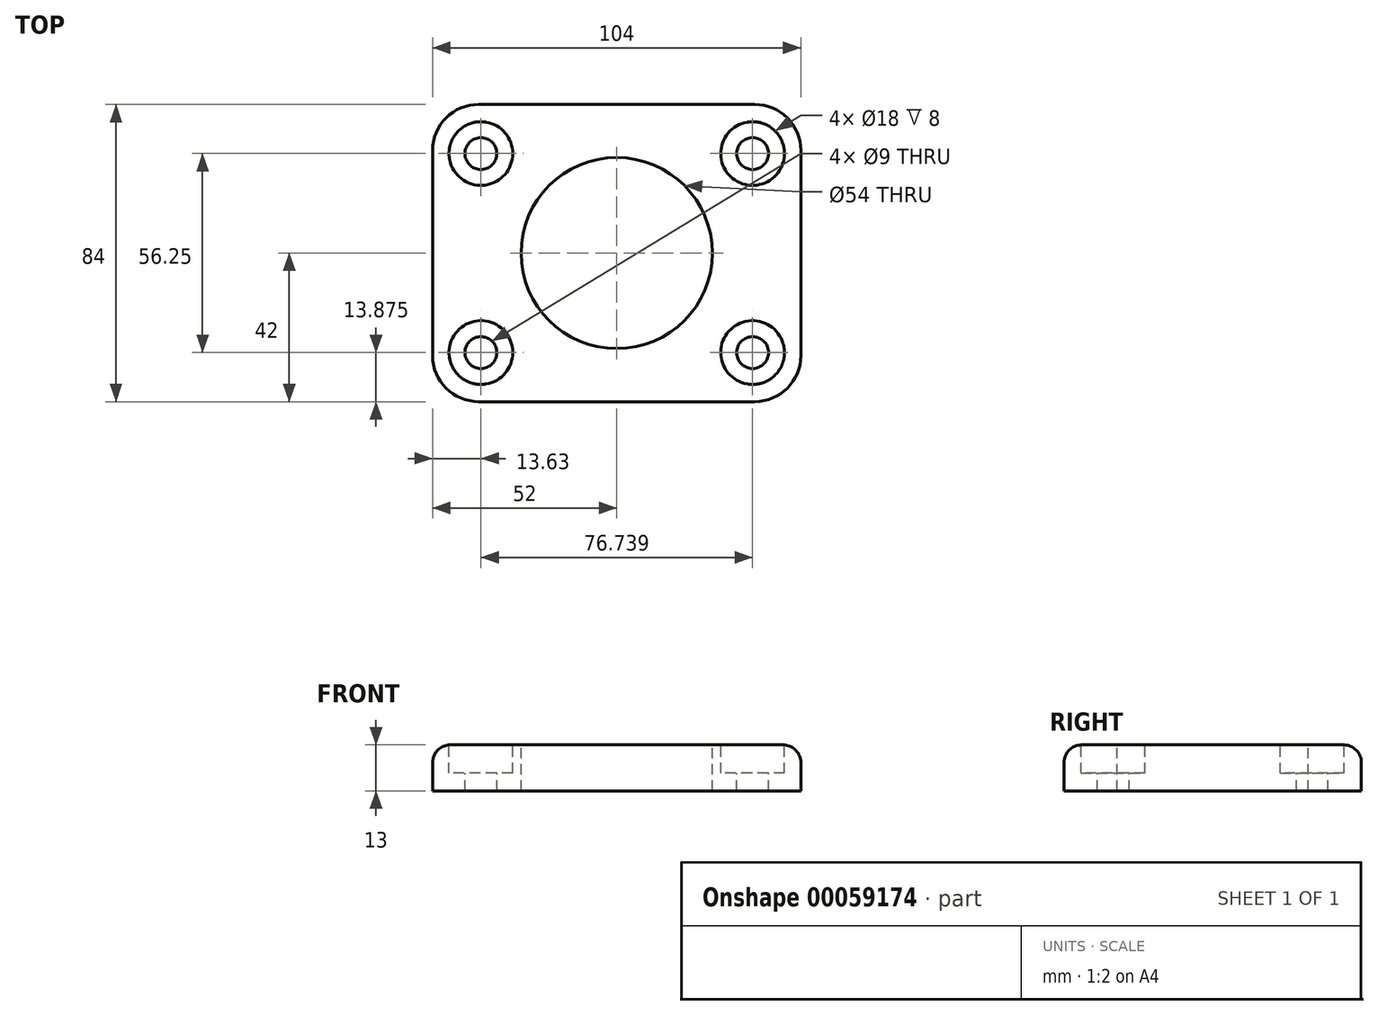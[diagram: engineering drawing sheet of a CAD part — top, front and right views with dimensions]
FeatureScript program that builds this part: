
annotation { "Feature Type Name" : "Feature", "Feature Type Description" : "" }
export const myFeature = defineFeature(function(context is Context, id is Id, definition is map)
    precondition{}
    {
        {
            var Q0;
            Q0=qCreatedBy(makeId("Top.planeOp"),FACE);
            var sketch = newSketch(context, id + "F0", { "sketchPlane" : qUnion([Q0])});
            skLineSegment(sketch, "E0.rect.bottom", {"start": v(52, 42) * mm, "end": v(-52, 42) * mm});
            skLineSegment(sketch, "E0.rect.top", {"start": v(52, -42) * mm, "end": v(-52, -42) * mm});
            skLineSegment(sketch, "E0.rect.left", {"start": v(52, 42) * mm, "end": v(52, -42) * mm});
            skLineSegment(sketch, "E0.rect.right", {"start": v(-52, 42) * mm, "end": v(-52, -42) * mm});
            skPoint(sketch, "E0.rect.middle", {"position": v(0, 0) * mm});
            skPoint(sketch, "E1", {"position": v(32, 27) * mm});
            skSolve(sketch);
        }
        {
            var Q0;
            Q0=makeQuery(id+"F0.imprint","IMPRINT",FACE,{"disambiguationData":[TD([[makeQuery(id+"F0.imprint","IMPRINT",EDGE,{"derivedFrom":sQuery(id+"F0.wireOp",EDGE,"E0.rect.bottom")}),1.0]])]});
            extrude(context, id + "F1", {"entities" : qUnion([Q0]), "oppositeDirection" : true, "depth" : 13 * mm});
        }
        {
            var Q0;
            Q0=makeQuery(id+"F1.opExtrude","CAP_FACE",FACE,{"disambiguationData":[OSD([sQuery(id+"F0.wireOp",EDGE,"E0.rect.bottom"),sQuery(id+"F0.wireOp",EDGE,"E0.rect.top"),sQuery(id+"F0.wireOp",EDGE,"E0.rect.left"),sQuery(id+"F0.wireOp",EDGE,"E0.rect.right")])],"isStart":true});
            var sketch = newSketch(context, id + "F2", { "sketchPlane" : qUnion([Q0])});
            skLineSegment(sketch, "E2", {"start": v(35.49, 25) * mm, "end": v(41.25, 31.25) * mm});
            skArc(sketch, "E3.0.startCap", {"start": v(38.8, 21.95) * mm, "mid": v(32.44, 21.7) * mm, "end": v(32.18, 28.05) * mm});
            skArc(sketch, "E3.0.endCap", {"start": v(37.94, 34.3) * mm, "mid": v(44.3, 34.56) * mm, "end": v(44.56, 28.2) * mm});
            skLineSegment(sketch, "E3.0.left", {"start": v(32.18, 28.05) * mm, "end": v(37.94, 34.3) * mm});
            skLineSegment(sketch, "E3.0.right", {"start": v(38.8, 21.95) * mm, "end": v(44.56, 28.2) * mm});
            skArc(sketch, "E4.MirrorCS", {"start": v(38.8, -21.95) * mm, "mid": v(32.44, -21.7) * mm, "end": v(32.18, -28.05) * mm});
            skLineSegment(sketch, "E5.MirrorCS", {"start": v(35.49, -25) * mm, "end": v(41.25, -31.25) * mm});
            skLineSegment(sketch, "E6.MirrorCS", {"start": v(32.18, -28.05) * mm, "end": v(37.94, -34.3) * mm});
            skLineSegment(sketch, "E7.MirrorCS", {"start": v(38.8, -21.95) * mm, "end": v(44.56, -28.2) * mm});
            skArc(sketch, "E8.MirrorCS", {"start": v(37.94, -34.3) * mm, "mid": v(44.3, -34.56) * mm, "end": v(44.56, -28.2) * mm});
            skLineSegment(sketch, "E9.MirrorCS", {"start": v(-38.8, -21.95) * mm, "end": v(-44.56, -28.2) * mm});
            skArc(sketch, "E10.MirrorCS", {"start": v(-37.94, -34.3) * mm, "mid": v(-44.3, -34.56) * mm, "end": v(-44.56, -28.2) * mm});
            skLineSegment(sketch, "E11.MirrorCS", {"start": v(-32.18, -28.05) * mm, "end": v(-37.94, -34.3) * mm});
            skArc(sketch, "E12.MirrorCS", {"start": v(-37.94, 34.3) * mm, "mid": v(-44.3, 34.56) * mm, "end": v(-44.56, 28.2) * mm});
            skLineSegment(sketch, "E13.MirrorCS", {"start": v(-35.49, -25) * mm, "end": v(-41.25, -31.25) * mm});
            skLineSegment(sketch, "E14.MirrorCS", {"start": v(-35.49, 25) * mm, "end": v(-41.25, 31.25) * mm});
            skArc(sketch, "E15.MirrorCS", {"start": v(-38.8, 21.95) * mm, "mid": v(-32.44, 21.7) * mm, "end": v(-32.18, 28.05) * mm});
            skArc(sketch, "E16.MirrorCS", {"start": v(-38.8, -21.95) * mm, "mid": v(-32.44, -21.7) * mm, "end": v(-32.18, -28.05) * mm});
            skLineSegment(sketch, "E17.MirrorCS", {"start": v(-38.8, 21.95) * mm, "end": v(-44.56, 28.2) * mm});
            skLineSegment(sketch, "E18.MirrorCS", {"start": v(-32.18, 28.05) * mm, "end": v(-37.94, 34.3) * mm});
            skSolve(sketch);
        }
        {
            var Q0;
            Q0=qCreatedBy(makeId("Top.planeOp"),FACE);
            var sketch = newSketch(context, id + "F3", { "sketchPlane" : qUnion([Q0])});
            skCircle(sketch, "E19", {"center": v(38.37, 28.13) * mm, "radius": 9 * mm});
            skCircle(sketch, "E20", {"center": v(38.37, -28.13) * mm, "radius": 9 * mm});
            skCircle(sketch, "E21", {"center": v(-38.37, 28.13) * mm, "radius": 9 * mm});
            skCircle(sketch, "E22", {"center": v(-38.37, -28.13) * mm, "radius": 9 * mm});
            skSolve(sketch);
        }
        {
            var Q0;
            Q0 = qSketchRegion(id + "F3", true);
            extrude(context, id + "F4", {"entities" : qUnion([Q0]), "operationType" : NewBodyOperationType.REMOVE, "oppositeDirection" : true, "depth" : 8 * mm});
        }
        {
            var Q0;
            Q0=makeQuery(id+"F4.boolean.opBoolean","COPY",FACE,{"derivedFrom":makeQuery(id+"F4.opExtrude","CAP_FACE",FACE,{"disambiguationData":[OSD([sQuery(id+"F3.wireOp",EDGE,"E19")])],"isStart":false})});
            var sketch = newSketch(context, id + "F5", { "sketchPlane" : qUnion([Q0])});
            skCircle(sketch, "E23", {"center": v(38.37, 28.13) * mm, "radius": 4.5 * mm});
            skCircle(sketch, "E24", {"center": v(38.37, -28.13) * mm, "radius": 4.5 * mm});
            skCircle(sketch, "E25", {"center": v(-38.37, 28.13) * mm, "radius": 4.5 * mm});
            skCircle(sketch, "E26", {"center": v(-38.37, -28.13) * mm, "radius": 4.5 * mm});
            skSolve(sketch);
        }
        {
            var Q0;
            Q0 = qSketchRegion(id + "F5", true);
            extrude(context, id + "F6", {"entities" : qUnion([Q0]), "operationType" : NewBodyOperationType.REMOVE, "oppositeDirection" : true, "depth" : 25 * mm});
        }
        {
            var Q0;
            Q0=qCreatedBy(makeId("Top.planeOp"),FACE);
            var sketch = newSketch(context, id + "F7", { "sketchPlane" : qUnion([Q0])});
            skCircle(sketch, "E27", {"center": v(0, 0) * mm, "radius": 27 * mm});
            skSolve(sketch);
        }
        {
            var Q0;
            Q0 = qSketchRegion(id + "F7", true);
            extrude(context, id + "F8", {"entities" : qUnion([Q0]), "operationType" : NewBodyOperationType.REMOVE, "oppositeDirection" : true, "depth" : 25 * mm});
        }
        {
            var Q0;
            Q0=makeQuery(id+"F1.opExtrude","SWEPT_EDGE",EDGE,{"disambiguationData":[OSD([sQuery(id+"F0.wireOp",EDGE,"E0.rect.bottom"),sQuery(id+"F0.wireOp",EDGE,"E0.rect.right")])]});
            var Q1;
            Q1=makeQuery(id+"F1.opExtrude","SWEPT_EDGE",EDGE,{"disambiguationData":[OSD([sQuery(id+"F0.wireOp",EDGE,"E0.rect.top"),sQuery(id+"F0.wireOp",EDGE,"E0.rect.right")])]});
            var Q2;
            Q2=makeQuery(id+"F1.opExtrude","SWEPT_EDGE",EDGE,{"disambiguationData":[OSD([sQuery(id+"F0.wireOp",EDGE,"E0.rect.top"),sQuery(id+"F0.wireOp",EDGE,"E0.rect.left")])]});
            var Q3;
            Q3=makeQuery(id+"F1.opExtrude","SWEPT_EDGE",EDGE,{"disambiguationData":[OSD([sQuery(id+"F0.wireOp",EDGE,"E0.rect.bottom"),sQuery(id+"F0.wireOp",EDGE,"E0.rect.left")])]});
            fillet(context, id + "F9", {"entities" : qUnion([Q0, Q1, Q2, Q3]), "radius" : 13 * mm, "tangentPropagation" : true, "allowEdgeOverflow" : false});
        }
        {
            var Q0;
            Q0=makeQuery(id+"F1.opExtrude","CAP_EDGE",EDGE,{"disambiguationData":[OSD([sQuery(id+"F0.wireOp",EDGE,"E0.rect.right")])],"isStart":true});
            fillet(context, id + "F10", {"entities" : qUnion([Q0]), "radius" : 5 * mm, "tangentPropagation" : true, "allowEdgeOverflow" : false});
        }
    });
